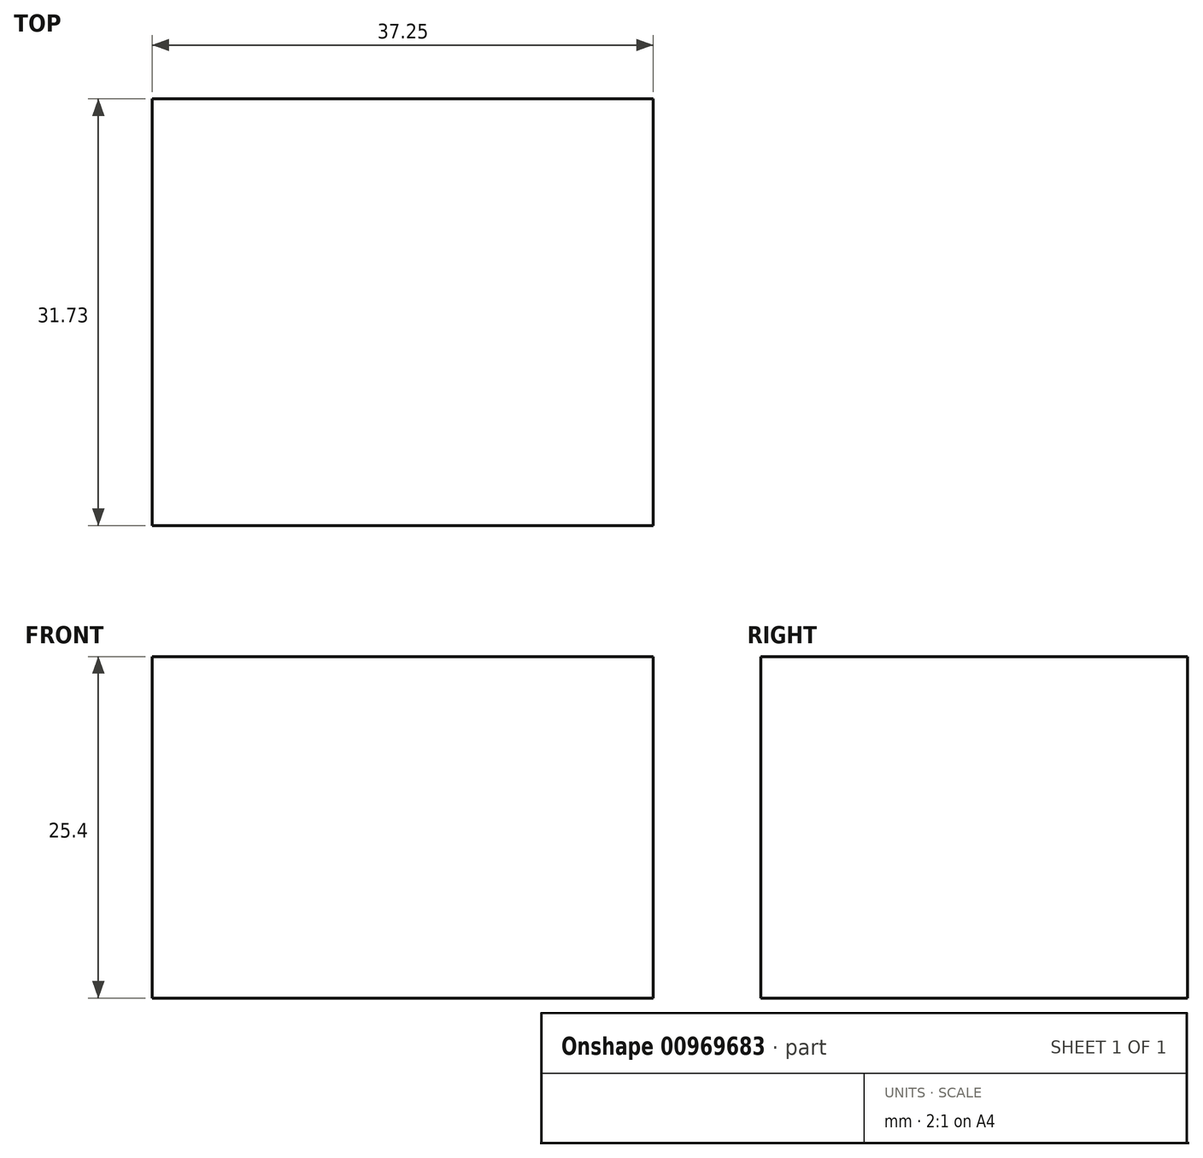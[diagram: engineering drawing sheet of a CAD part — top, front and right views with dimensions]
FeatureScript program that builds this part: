
annotation { "Feature Type Name" : "Feature", "Feature Type Description" : "" }
export const myFeature = defineFeature(function(context is Context, id is Id, definition is map)
    precondition{}
    {
        {
            var Q0;
            Q0=qCreatedBy(makeId("Top.planeOp"),FACE);
            var sketch = newSketch(context, id + "F0", { "sketchPlane" : qUnion([Q0])});
            skLineSegment(sketch, "E0.bottom", {"start": v(0, 0) * mm, "end": v(37.25, 0) * mm});
            skLineSegment(sketch, "E0.top", {"start": v(0, 31.73) * mm, "end": v(37.25, 31.73) * mm});
            skLineSegment(sketch, "E0.left", {"start": v(0, 0) * mm, "end": v(0, 31.73) * mm});
            skLineSegment(sketch, "E0.right", {"start": v(37.25, 0) * mm, "end": v(37.25, 31.73) * mm});
            skSolve(sketch);
        }
        {
            var Q0;
            Q0 = qSketchRegion(id + "F0", true);
            extrude(context, id + "F1", {"entities" : qUnion([Q0]), "depth" : 25.4 * mm, "offsetDistance" : 25.4 * mm});
        }
    });
